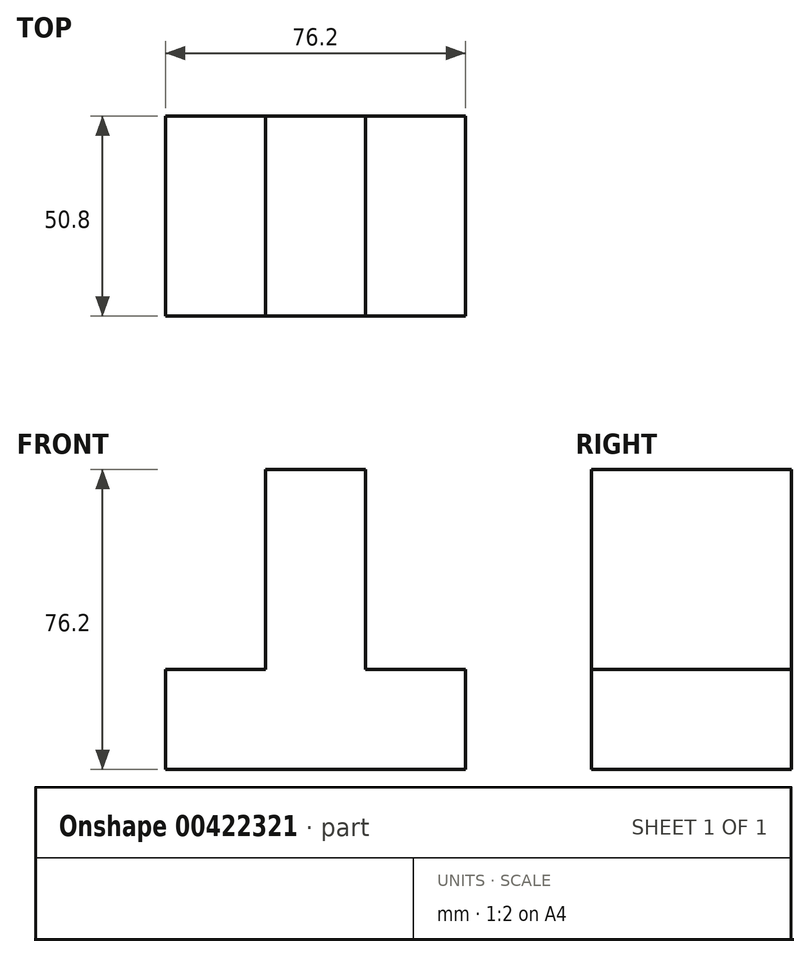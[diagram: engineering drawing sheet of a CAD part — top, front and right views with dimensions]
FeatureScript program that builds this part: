
annotation { "Feature Type Name" : "Feature", "Feature Type Description" : "" }
export const myFeature = defineFeature(function(context is Context, id is Id, definition is map)
    precondition{}
    {
        {
            var Q0;
            Q0=qCreatedBy(makeId("Front.planeOp"),FACE);
            var sketch = newSketch(context, id + "F0", { "sketchPlane" : qUnion([Q0])});
            skLineSegment(sketch, "E0", {"start": v(-66.24, -55.86) * mm, "end": v(-66.24, -30.46) * mm});
            skLineSegment(sketch, "E1", {"start": v(-66.24, -30.46) * mm, "end": v(-40.84, -30.46) * mm});
            skLineSegment(sketch, "E2", {"start": v(-40.84, -30.46) * mm, "end": v(-40.84, 20.34) * mm});
            skLineSegment(sketch, "E3", {"start": v(-40.84, 20.34) * mm, "end": v(-15.44, 20.34) * mm});
            skLineSegment(sketch, "E4", {"start": v(-15.44, 20.34) * mm, "end": v(-15.44, -30.46) * mm});
            skLineSegment(sketch, "E5", {"start": v(-15.44, -30.46) * mm, "end": v(9.96, -30.46) * mm});
            skLineSegment(sketch, "E6", {"start": v(-66.24, -55.86) * mm, "end": v(9.96, -55.86) * mm});
            skLineSegment(sketch, "E7", {"start": v(9.96, -30.46) * mm, "end": v(9.96, -55.86) * mm});
            skSolve(sketch);
        }
        {
            var Q0;
            Q0=makeQuery(id+"F0.imprint","IMPRINT",FACE,{"disambiguationData":[TD([[makeQuery(id+"F0.imprint","IMPRINT",EDGE,{"derivedFrom":sQuery(id+"F0.wireOp",EDGE,"E0")}),-1.0]])]});
            extrude(context, id + "F1", {"entities" : qUnion([Q0]), "depth" : 50.8 * mm});
        }
    });
